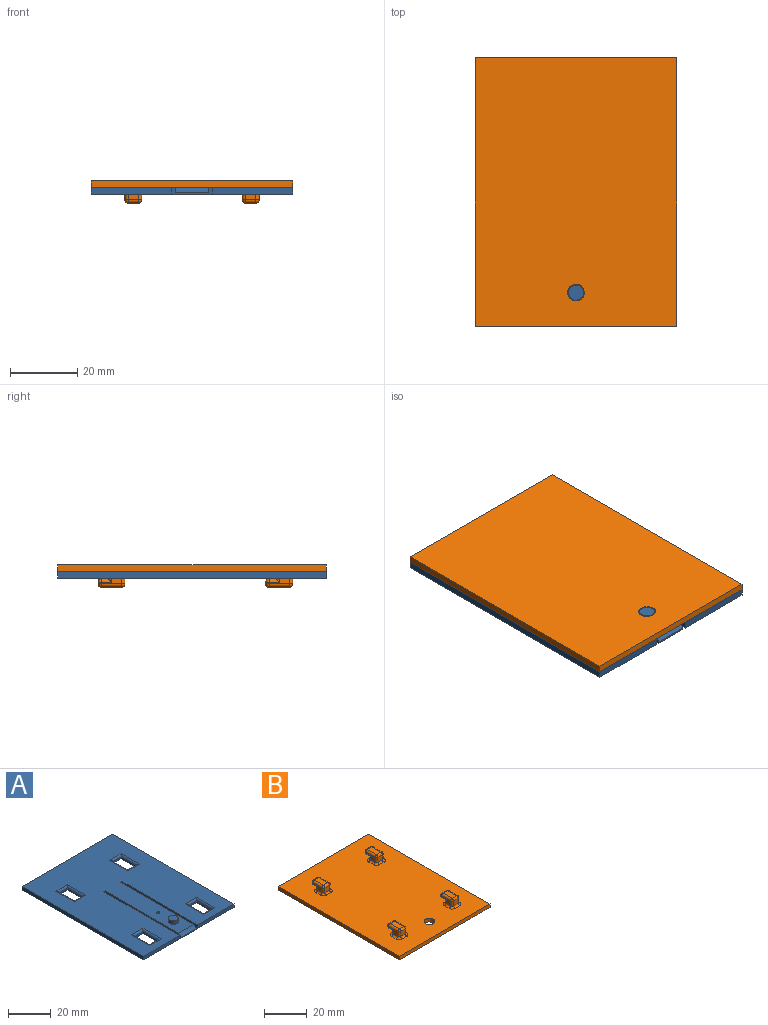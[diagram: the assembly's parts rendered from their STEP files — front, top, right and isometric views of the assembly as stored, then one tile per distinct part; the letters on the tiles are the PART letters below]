
ASSEMBLY  parts=2 mates=1
PART A: 50 faces, bbox 60x80x4 mm
  f0: plane 5.5x1mm, normal (0,-1,0), area 5.5mm2, adj f1,f28,f30,f34
  f1: plane 10x1mm, normal (-1,0,0), area 10mm2, adj f0,f2,f30,f35
  f2: plane 5.5x1mm, normal (0,1,0), area 5.5mm2, adj f1,f28,f30,f37
  f3: plane 5.5x1mm, normal (0,-1,0), area 5.5mm2, adj f4,f23,f30,f39
  f4: plane 10x1mm, normal (-1,0,0), area 10mm2, adj f3,f5,f30,f38
  f5: plane 5.5x1mm, normal (0,1,0), area 5.5mm2, adj f4,f23,f30,f40
  f6: plane 10x1mm, normal (1,0,0), area 10mm2, adj f7,f25,f30,f43
  f7: plane 5.5x1mm, normal (0,-1,0), area 5.5mm2, adj f6,f8,f30,f42
  f8: plane 10x1mm, normal (-1,0,0), area 10mm2, adj f7,f25,f30,f44
  f9: plane 10x1mm, normal (1,0,0), area 10mm2, adj f10,f26,f30,f47
  f10: plane 5.5x1mm, normal (0,-1,0), area 5.5mm2, adj f9,f11,f30,f46
  f11: plane 10x1mm, normal (-1,0,0), area 10mm2, adj f10,f26,f30,f48
  f12: plane 50x2mm, normal (-1,0,0), area 100mm2, adj f13,f27,f29,f30
  f13: plane 24x2mm, normal (0,-1,0), area 48mm2, adj f12,f14,f29,f30
  f14: plane 80x2mm, normal (1,0,0), area 160mm2, adj f13,f15,f29,f30
  f15: plane 60x2mm, normal (0,1,0), area 120mm2, adj f14,f16,f29,f30
  f16: plane 80x2mm, normal (-1,0,0), area 160mm2, adj f15,f17,f29,f30
  f17: plane 24x2mm, normal (0,-1,0), area 48mm2, adj f16,f18,f29,f30
  f18: plane 50x2mm, normal (1,0,0), area 100mm2, adj f17,f19,f29,f30
  f19: plane 2x1mm, normal (0,-1,0), area 2mm2, adj f18,f20,f29,f30
  f20: plane 50x2mm, normal (-1,0,0), area 98.9mm2, adj f19,f21,f29,f30,f33
  f21: plane 10x0.5mm, normal (0,-1,0), area 5mm2, adj f20,f22,f30,f33
  f22: plane 50x2mm, normal (1,0,0), area 98.9mm2, adj f21,f27,f29,f30,f33
  f23: plane 10x1mm, normal (1,0,0), area 10mm2, adj f3,f5,f30,f41
  f24: cylinder r=0.75mm len=2mm, axis (0,0,-1), area 9.4mm2, adj f29,f30
  f25: plane 5.5x1mm, normal (0,1,0), area 5.5mm2, adj f6,f8,f30,f45
  f26: plane 5.5x1mm, normal (0,1,0), area 5.5mm2, adj f9,f11,f30,f49
  f27: plane 2x1mm, normal (0,-1,0), area 2mm2, adj f12,f22,f29,f30
  f28: plane 10x1mm, normal (1,0,0), area 10mm2, adj f0,f2,f30,f36
  f29: plane 80x60mm, normal (0,0,1), area 4307.3mm2, adj f12,f13,f14,f15,f16,f17,f18,f19
  f30: plane 80x60mm, normal (0,0,-1), area 4478.2mm2, adj f0,f1,f2,f3,f4,f5,f6,f7
  f31: cylinder r=2.25mm len=4.5mm, axis (0,0,-1), area 28.3mm2, adj f29,f32
  f32: plane 4.5x4.5mm, normal (0,0,1), area 15.9mm2, adj f31
  f33: plane 10x1.5mm, normal (0,-0.71,0.71), area 21.2mm2, adj f20,f21,f22,f29
  f34: cylinder r=1mm len=7.5mm, axis (-1,0,0), area 9.8mm2, adj f0,f29,f35,f36
  f35: cylinder r=1mm len=12mm, axis (0,1,0), area 16.8mm2, adj f1,f29,f34,f37
  f36: cylinder r=1mm len=12mm, axis (0,-1,0), area 16.8mm2, adj f28,f29,f34,f37
  f37: cylinder r=1mm len=7.5mm, axis (1,0,0), area 9.8mm2, adj f2,f29,f35,f36
  f38: cylinder r=1mm len=12mm, axis (0,1,0), area 16.8mm2, adj f4,f29,f39,f40
  f39: cylinder r=1mm len=7.5mm, axis (-1,0,0), area 9.8mm2, adj f3,f29,f38,f41
  f40: cylinder r=1mm len=7.5mm, axis (1,0,0), area 9.8mm2, adj f5,f29,f38,f41
  f41: cylinder r=1mm len=12mm, axis (0,-1,0), area 16.8mm2, adj f23,f29,f39,f40
  f42: cylinder r=1mm len=7.5mm, axis (-1,0,0), area 9.8mm2, adj f7,f29,f43,f44
  f43: cylinder r=1mm len=12mm, axis (0,-1,0), area 16.8mm2, adj f6,f29,f42,f45
  f44: cylinder r=1mm len=12mm, axis (0,1,0), area 16.8mm2, adj f8,f29,f42,f45
  f45: cylinder r=1mm len=7.5mm, axis (1,0,0), area 9.8mm2, adj f25,f29,f43,f44
  f46: cylinder r=1mm len=7.5mm, axis (-1,0,0), area 9.8mm2, adj f10,f29,f47,f48
  f47: cylinder r=1mm len=12mm, axis (0,-1,0), area 16.8mm2, adj f9,f29,f46,f49
  f48: cylinder r=1mm len=12mm, axis (0,1,0), area 16.8mm2, adj f11,f29,f46,f49
  f49: cylinder r=1mm len=7.5mm, axis (1,0,0), area 9.8mm2, adj f26,f29,f47,f48
PART B: 143 faces, bbox 60x80x6.7 mm
  f0: plane 80x60mm, normal (0,0,1), area 4598.1mm2, adj f1,f2,f3,f4,f5,f35,f36,f37
  f1: plane 60x2mm, normal (0,-1,0), area 120mm2, adj f0,f2,f5,f6
  f2: plane 80x2mm, normal (1,0,0), area 160mm2, adj f0,f1,f3,f6
  f3: plane 60x2mm, normal (0,1,0), area 120mm2, adj f0,f2,f5,f6
  f4: cylinder r=2.5mm len=5mm, axis (0,0,-1), area 31.4mm2, adj f0,f6
  f5: plane 80x2mm, normal (-1,0,0), area 160mm2, adj f0,f1,f3,f6
  f6: plane 80x60mm, normal (0,0,-1), area 4780.4mm2, adj f1,f2,f3,f4,f5
  f7: plane 3x1.2mm, normal (0,1,0), area 3.6mm2, adj f25,f42,f43,f54
  f8: plane 6x2.7mm, normal (-1,0,0), area 9.6mm2, adj f36,f38,f42,f47,f48,f49
  f9: plane 3x2.7mm, normal (0,-1,0), area 8.1mm2, adj f37,f38,f45,f46
  f10: plane 6x2.7mm, normal (1,0,0), area 9.6mm2, adj f44,f45,f54,f55,f58,f61
  f11: plane 3x1.2mm, normal (0,1,0), area 3.6mm2, adj f28,f123,f124,f135
  f12: plane 6x2.7mm, normal (-1,0,0), area 9.6mm2, adj f117,f119,f123,f128,f129,f130
  f13: plane 3x2.7mm, normal (0,-1,0), area 8.1mm2, adj f118,f119,f126,f127
  f14: plane 6x2.7mm, normal (1,0,0), area 9.6mm2, adj f125,f126,f135,f136,f139,f142
  f15: plane 3x2.7mm, normal (0,-1,0), area 8.1mm2, adj f91,f92,f99,f100
  f16: plane 6x2.7mm, normal (1,0,0), area 9.6mm2, adj f98,f99,f108,f109,f112,f115
  f17: plane 3x1.2mm, normal (0,1,0), area 3.6mm2, adj f29,f96,f97,f108
  f18: plane 6x2.7mm, normal (-1,0,0), area 9.6mm2, adj f90,f92,f96,f101,f102,f103
  f19: plane 3x2.7mm, normal (0,-1,0), area 8.1mm2, adj f64,f65,f72,f73
  f20: plane 6x2.7mm, normal (1,0,0), area 9.6mm2, adj f71,f72,f81,f82,f85,f88
  f21: plane 3x1.2mm, normal (0,1,0), area 3.6mm2, adj f32,f69,f70,f81
  f22: plane 6x2.7mm, normal (-1,0,0), area 9.6mm2, adj f63,f65,f69,f74,f75,f76
  f23: plane 3x0.5mm, normal (0,1,0), area 1.5mm2, adj f48,f56,f57,f61
  f24: plane 6x3mm, normal (0,0,1), area 18mm2, adj f46,f47,f55,f56
  f25: plane 3x2mm, normal (0,0,-1), area 6mm2, adj f7,f49,f57,f58
  f26: plane 3x0.5mm, normal (0,1,0), area 1.5mm2, adj f129,f137,f138,f142
  f27: plane 6x3mm, normal (0,0,1), area 18mm2, adj f127,f128,f136,f137
  f28: plane 3x2mm, normal (0,0,-1), area 6mm2, adj f11,f130,f138,f139
  f29: plane 3x2mm, normal (0,0,-1), area 6mm2, adj f17,f103,f111,f112
  f30: plane 3x0.5mm, normal (0,1,0), area 1.5mm2, adj f102,f110,f111,f115
  f31: plane 6x3mm, normal (0,0,1), area 18mm2, adj f100,f101,f109,f110
  f32: plane 3x2mm, normal (0,0,-1), area 6mm2, adj f21,f76,f84,f85
  f33: plane 3x0.5mm, normal (0,1,0), area 1.5mm2, adj f75,f83,f84,f88
  f34: plane 6x3mm, normal (0,0,1), area 18mm2, adj f73,f74,f82,f83
  f35: torus R=2mm, axis (0,0,1), area 3.4mm2, adj f0,f36,f37,f38
  f36: cylinder r=1mm len=3mm, axis (0,-1,0), area 4.7mm2, adj f0,f8,f35,f39
  f37: cylinder r=1mm len=3mm, axis (1,0,0), area 4.7mm2, adj f0,f9,f35,f40
  f38: cylinder r=1mm len=2.7mm, axis (0,0,-1), area 4.2mm2, adj f8,f9,f35,f41
  f39: torus R=2mm, axis (0,0,1), area 3.4mm2, adj f0,f36,f42,f43
  f40: torus R=2mm, axis (0,0,1), area 3.4mm2, adj f0,f37,f44,f45
  f41: sphere r=1mm, area 1.6mm2, adj f38,f46,f47
  f42: cylinder r=1mm len=2.2mm, axis (0,0,1), area 2.5mm2, adj f7,f8,f39,f49
  f43: cylinder r=1mm len=3mm, axis (-1,0,0), area 4.7mm2, adj f0,f7,f39,f50
  f44: cylinder r=1mm len=3mm, axis (0,1,0), area 4.7mm2, adj f0,f10,f40,f50
  f45: cylinder r=1mm len=2.7mm, axis (0,0,1), area 4.2mm2, adj f9,f10,f40,f51
  f46: cylinder r=1mm len=3mm, axis (-1,0,0), area 4.7mm2, adj f9,f24,f41,f51
  f47: cylinder r=1mm len=6mm, axis (0,1,0), area 9.4mm2, adj f8,f24,f41,f52
  f48: cylinder r=1mm len=1mm, axis (0,0,1), area 0.8mm2, adj f8,f23,f52,f53
  f49: cylinder r=1mm len=3mm, axis (0,-1,0), area 3.7mm2, adj f8,f25,f42,f53
  f50: torus R=2mm, axis (0,0,1), area 3.4mm2, adj f0,f43,f44,f54
  f51: sphere r=1mm, area 1.6mm2, adj f45,f46,f55
  f52: sphere r=1mm, area 1.6mm2, adj f47,f48,f56
  f53: sphere r=1mm, area 1.6mm2, adj f48,f49,f57
  f54: cylinder r=1mm len=2.2mm, axis (0,0,-1), area 2.5mm2, adj f7,f10,f50,f58
  f55: cylinder r=1mm len=6mm, axis (0,-1,0), area 9.4mm2, adj f10,f24,f51,f59
  f56: cylinder r=1mm len=3mm, axis (1,0,0), area 4.7mm2, adj f23,f24,f52,f59
  f57: cylinder r=1mm len=3mm, axis (-1,0,0), area 4.7mm2, adj f23,f25,f53,f60
  f58: cylinder r=1mm len=3mm, axis (0,1,0), area 3.7mm2, adj f10,f25,f54,f60
  f59: sphere r=1mm, area 1.6mm2, adj f55,f56,f61
  f60: sphere r=1mm, area 1.6mm2, adj f57,f58,f61
  f61: cylinder r=1mm len=1mm, axis (0,0,-1), area 0.8mm2, adj f10,f23,f59,f60
  f62: torus R=2mm, axis (0,0,1), area 3.4mm2, adj f0,f63,f64,f65
  f63: cylinder r=1mm len=3mm, axis (0,-1,0), area 4.7mm2, adj f0,f22,f62,f66
  f64: cylinder r=1mm len=3mm, axis (1,0,0), area 4.7mm2, adj f0,f19,f62,f67
  f65: cylinder r=1mm len=2.7mm, axis (0,0,1), area 4.2mm2, adj f19,f22,f62,f68
  f66: torus R=2mm, axis (0,0,1), area 3.4mm2, adj f0,f63,f69,f70
  f67: torus R=2mm, axis (0,0,1), area 3.4mm2, adj f0,f64,f71,f72
  f68: sphere r=1mm, area 1.6mm2, adj f65,f73,f74
  f69: cylinder r=1mm len=2.2mm, axis (0,0,-1), area 2.5mm2, adj f21,f22,f66,f76
  f70: cylinder r=1mm len=3mm, axis (-1,0,0), area 4.7mm2, adj f0,f21,f66,f77
  f71: cylinder r=1mm len=3mm, axis (0,1,0), area 4.7mm2, adj f0,f20,f67,f77
  f72: cylinder r=1mm len=2.7mm, axis (0,0,-1), area 4.2mm2, adj f19,f20,f67,f78
  f73: cylinder r=1mm len=3mm, axis (-1,0,0), area 4.7mm2, adj f19,f34,f68,f78
  f74: cylinder r=1mm len=6mm, axis (0,-1,0), area 9.4mm2, adj f22,f34,f68,f79
  f75: cylinder r=1mm len=1mm, axis (0,0,-1), area 0.8mm2, adj f22,f33,f79,f80
  f76: cylinder r=1mm len=3mm, axis (0,1,0), area 3.7mm2, adj f22,f32,f69,f80
  f77: torus R=2mm, axis (0,0,1), area 3.4mm2, adj f0,f70,f71,f81
  f78: sphere r=1mm, area 1.6mm2, adj f72,f73,f82
  f79: sphere r=1mm, area 1.6mm2, adj f74,f75,f83
  f80: sphere r=1mm, area 1.6mm2, adj f75,f76,f84
  f81: cylinder r=1mm len=2.2mm, axis (0,0,1), area 2.5mm2, adj f20,f21,f77,f85
  f82: cylinder r=1mm len=6mm, axis (0,1,0), area 9.4mm2, adj f20,f34,f78,f86
  f83: cylinder r=1mm len=3mm, axis (1,0,0), area 4.7mm2, adj f33,f34,f79,f86
  f84: cylinder r=1mm len=3mm, axis (-1,0,0), area 4.7mm2, adj f32,f33,f80,f87
  f85: cylinder r=1mm len=3mm, axis (0,-1,0), area 3.7mm2, adj f20,f32,f81,f87
  f86: sphere r=1mm, area 1.6mm2, adj f82,f83,f88
  f87: sphere r=1mm, area 1.6mm2, adj f84,f85,f88
  f88: cylinder r=1mm len=1mm, axis (0,0,1), area 0.8mm2, adj f20,f33,f86,f87
  f89: torus R=2mm, axis (0,0,1), area 3.4mm2, adj f0,f90,f91,f92
  f90: cylinder r=1mm len=3mm, axis (0,-1,0), area 4.7mm2, adj f0,f18,f89,f93
  f91: cylinder r=1mm len=3mm, axis (1,0,0), area 4.7mm2, adj f0,f15,f89,f94
  f92: cylinder r=1mm len=2.7mm, axis (0,0,1), area 4.2mm2, adj f15,f18,f89,f95
  f93: torus R=2mm, axis (0,0,1), area 3.4mm2, adj f0,f90,f96,f97
  f94: torus R=2mm, axis (0,0,1), area 3.4mm2, adj f0,f91,f98,f99
  f95: sphere r=1mm, area 1.6mm2, adj f92,f100,f101
  f96: cylinder r=1mm len=2.2mm, axis (0,0,-1), area 2.5mm2, adj f17,f18,f93,f103
  f97: cylinder r=1mm len=3mm, axis (-1,0,0), area 4.7mm2, adj f0,f17,f93,f104
  f98: cylinder r=1mm len=3mm, axis (0,1,0), area 4.7mm2, adj f0,f16,f94,f104
  f99: cylinder r=1mm len=2.7mm, axis (0,0,-1), area 4.2mm2, adj f15,f16,f94,f105
  f100: cylinder r=1mm len=3mm, axis (-1,0,0), area 4.7mm2, adj f15,f31,f95,f105
  f101: cylinder r=1mm len=6mm, axis (0,-1,0), area 9.4mm2, adj f18,f31,f95,f106
  f102: cylinder r=1mm len=1mm, axis (0,0,-1), area 0.8mm2, adj f18,f30,f106,f107
  f103: cylinder r=1mm len=3mm, axis (0,1,0), area 3.7mm2, adj f18,f29,f96,f107
  f104: torus R=2mm, axis (0,0,1), area 3.4mm2, adj f0,f97,f98,f108
  f105: sphere r=1mm, area 1.6mm2, adj f99,f100,f109
  f106: sphere r=1mm, area 1.6mm2, adj f101,f102,f110
  f107: sphere r=1mm, area 1.6mm2, adj f102,f103,f111
  f108: cylinder r=1mm len=2.2mm, axis (0,0,1), area 2.5mm2, adj f16,f17,f104,f112
  f109: cylinder r=1mm len=6mm, axis (0,1,0), area 9.4mm2, adj f16,f31,f105,f113
  f110: cylinder r=1mm len=3mm, axis (1,0,0), area 4.7mm2, adj f30,f31,f106,f113
  f111: cylinder r=1mm len=3mm, axis (-1,0,0), area 4.7mm2, adj f29,f30,f107,f114
  f112: cylinder r=1mm len=3mm, axis (0,-1,0), area 3.7mm2, adj f16,f29,f108,f114
  f113: sphere r=1mm, area 1.6mm2, adj f109,f110,f115
  f114: sphere r=1mm, area 1.6mm2, adj f111,f112,f115
  f115: cylinder r=1mm len=1mm, axis (0,0,1), area 0.8mm2, adj f16,f30,f113,f114
  f116: torus R=2mm, axis (0,0,1), area 3.4mm2, adj f0,f117,f118,f119
  f117: cylinder r=1mm len=3mm, axis (0,-1,0), area 4.7mm2, adj f0,f12,f116,f120
  f118: cylinder r=1mm len=3mm, axis (1,0,0), area 4.7mm2, adj f0,f13,f116,f121
  f119: cylinder r=1mm len=2.7mm, axis (0,0,-1), area 4.2mm2, adj f12,f13,f116,f122
  f120: torus R=2mm, axis (0,0,1), area 3.4mm2, adj f0,f117,f123,f124
  f121: torus R=2mm, axis (0,0,1), area 3.4mm2, adj f0,f118,f125,f126
  f122: sphere r=1mm, area 1.6mm2, adj f119,f127,f128
  f123: cylinder r=1mm len=2.2mm, axis (0,0,1), area 2.5mm2, adj f11,f12,f120,f130
  f124: cylinder r=1mm len=3mm, axis (-1,0,0), area 4.7mm2, adj f0,f11,f120,f131
  f125: cylinder r=1mm len=3mm, axis (0,1,0), area 4.7mm2, adj f0,f14,f121,f131
  f126: cylinder r=1mm len=2.7mm, axis (0,0,1), area 4.2mm2, adj f13,f14,f121,f132
  f127: cylinder r=1mm len=3mm, axis (-1,0,0), area 4.7mm2, adj f13,f27,f122,f132
  f128: cylinder r=1mm len=6mm, axis (0,-1,0), area 9.4mm2, adj f12,f27,f122,f133
  f129: cylinder r=1mm len=1mm, axis (0,0,1), area 0.8mm2, adj f12,f26,f133,f134
  f130: cylinder r=1mm len=3mm, axis (0,1,0), area 3.7mm2, adj f12,f28,f123,f134
  f131: torus R=2mm, axis (0,0,1), area 3.4mm2, adj f0,f124,f125,f135
  f132: sphere r=1mm, area 1.6mm2, adj f126,f127,f136
  f133: sphere r=1mm, area 1.6mm2, adj f128,f129,f137
  f134: sphere r=1mm, area 1.6mm2, adj f129,f130,f138
  f135: cylinder r=1mm len=2.2mm, axis (0,0,-1), area 2.5mm2, adj f11,f14,f131,f139
  f136: cylinder r=1mm len=6mm, axis (0,1,0), area 9.4mm2, adj f14,f27,f132,f140
  f137: cylinder r=1mm len=3mm, axis (1,0,0), area 4.7mm2, adj f26,f27,f133,f140
  f138: cylinder r=1mm len=3mm, axis (-1,0,0), area 4.7mm2, adj f26,f28,f134,f141
  f139: cylinder r=1mm len=3mm, axis (0,-1,0), area 3.7mm2, adj f14,f28,f135,f141
  f140: sphere r=1mm, area 1.6mm2, adj f136,f137,f142
  f141: sphere r=1mm, area 1.6mm2, adj f138,f139,f142
  f142: cylinder r=1mm len=1mm, axis (0,0,-1), area 0.8mm2, adj f14,f26,f140,f141
PLACE A t=(-33.33,0,26.84)mm
PLACE B rot(axis=(0,-1,0),180deg) t=(-33.33,0,30.84)mm
MATE planar A.f29 <-> B.f0  axis (0,0,-1) through (-3.33,-40,28.84)mm
